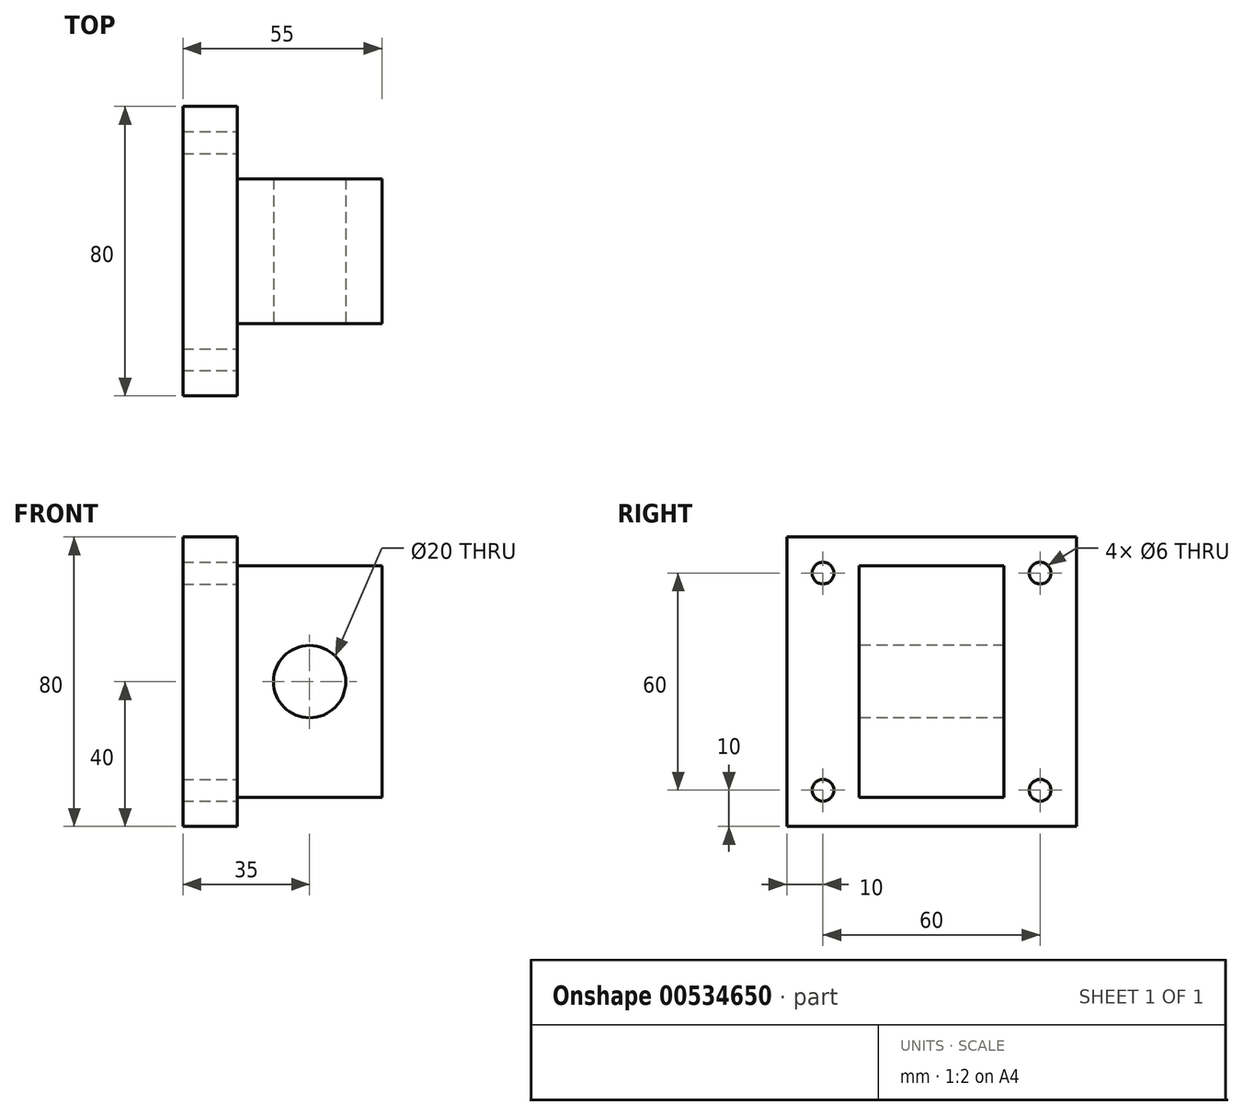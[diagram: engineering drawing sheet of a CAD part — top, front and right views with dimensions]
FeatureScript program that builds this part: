
annotation { "Feature Type Name" : "Feature", "Feature Type Description" : "" }
export const myFeature = defineFeature(function(context is Context, id is Id, definition is map)
    precondition{}
    {
        {
            var Q0;
            Q0=qCreatedBy(makeId("Right.planeOp"),FACE);
            var sketch = newSketch(context, id + "F0", { "sketchPlane" : qUnion([Q0])});
            skLineSegment(sketch, "E0.bottom", {"start": v(-40, 40) * mm, "end": v(40, 40) * mm});
            skLineSegment(sketch, "E0.top", {"start": v(-40, -40) * mm, "end": v(40, -40) * mm});
            skLineSegment(sketch, "E0.left", {"start": v(-40, 40) * mm, "end": v(-40, -40) * mm});
            skLineSegment(sketch, "E0.right", {"start": v(40, 40) * mm, "end": v(40, -40) * mm});
            skCircle(sketch, "E1", {"center": v(-30, 30) * mm, "radius": 3 * mm});
            skCircle(sketch, "E2", {"center": v(-30, -30) * mm, "radius": 3 * mm});
            skCircle(sketch, "E3", {"center": v(30, -30) * mm, "radius": 3 * mm});
            skCircle(sketch, "E4", {"center": v(30, 30) * mm, "radius": 3 * mm});
            skLineSegment(sketch, "E5.bottom", {"start": v(-20, 32) * mm, "end": v(20, 32) * mm});
            skLineSegment(sketch, "E5.top", {"start": v(-20, -32) * mm, "end": v(20, -32) * mm});
            skLineSegment(sketch, "E5.left", {"start": v(-20, 32) * mm, "end": v(-20, -32) * mm});
            skLineSegment(sketch, "E5.right", {"start": v(20, 32) * mm, "end": v(20, -32) * mm});
            skSolve(sketch);
        }
        {
            var Q0;
            Q0=makeQuery(id+"F0.imprint","IMPRINT",FACE,{"disambiguationData":[TD([[makeQuery(id+"F0.imprint","IMPRINT",EDGE,{"derivedFrom":sQuery(id+"F0.wireOp",EDGE,"E0.bottom")}),-1.0]])]});
            var Q1;
            Q1=makeQuery(id+"F0.imprint","IMPRINT",FACE,{"disambiguationData":[TD([[makeQuery(id+"F0.imprint","IMPRINT",EDGE,{"derivedFrom":sQuery(id+"F0.wireOp",EDGE,"u0jMUKhl-6n2V-fjkC-5YLW-VTPPdpPOOKdY")}),1.0]])]});
            var Q2;
            Q2=makeQuery(id+"F0.imprint","IMPRINT",FACE,{"disambiguationData":[TD([[makeQuery(id+"F0.imprint","IMPRINT",EDGE,{"derivedFrom":sQuery(id+"F0.wireOp",EDGE,"E5.bottom")}),-1.0]])]});
            extrude(context, id + "F1", {"entities" : qUnion([Q0, Q1, Q2]), "oppositeDirection" : true, "depth" : 15 * mm, "offsetDistance" : 25 * mm});
        }
        {
            var Q0;
            Q0=makeQuery(id+"F0.imprint","IMPRINT",FACE,{"disambiguationData":[TD([[makeQuery(id+"F0.imprint","IMPRINT",EDGE,{"derivedFrom":sQuery(id+"F0.wireOp",EDGE,"E5.bottom")}),-1.0]])]});
            extrude(context, id + "F2", {"entities" : qUnion([Q0]), "operationType" : NewBodyOperationType.ADD, "depth" : 40 * mm, "offsetDistance" : 25 * mm});
        }
        {
            var Q0;
            Q0=makeQuery(id+"F2.opExtrude","SWEPT_FACE",FACE,{"disambiguationData":[OSD([sQuery(id+"F0.wireOp",EDGE,"E5.left")])]});
            var sketch = newSketch(context, id + "F3", { "sketchPlane" : qUnion([Q0])});
            skCircle(sketch, "E6", {"center": v(20, 0) * mm, "radius": 10 * mm});
            skPoint(sketch, "E6.centerSnap0", {"position": v(20, 32) * mm});
            skSolve(sketch);
        }
        {
            var Q0;
            Q0 = qSketchRegion(id + "F3", true);
            extrude(context, id + "F4", {"entities" : qUnion([Q0]), "operationType" : NewBodyOperationType.REMOVE, "endBound" : BoundingType.THROUGH_ALL, "oppositeDirection" : true, "depth" : 25 * mm, "offsetDistance" : 25 * mm});
        }
    });
